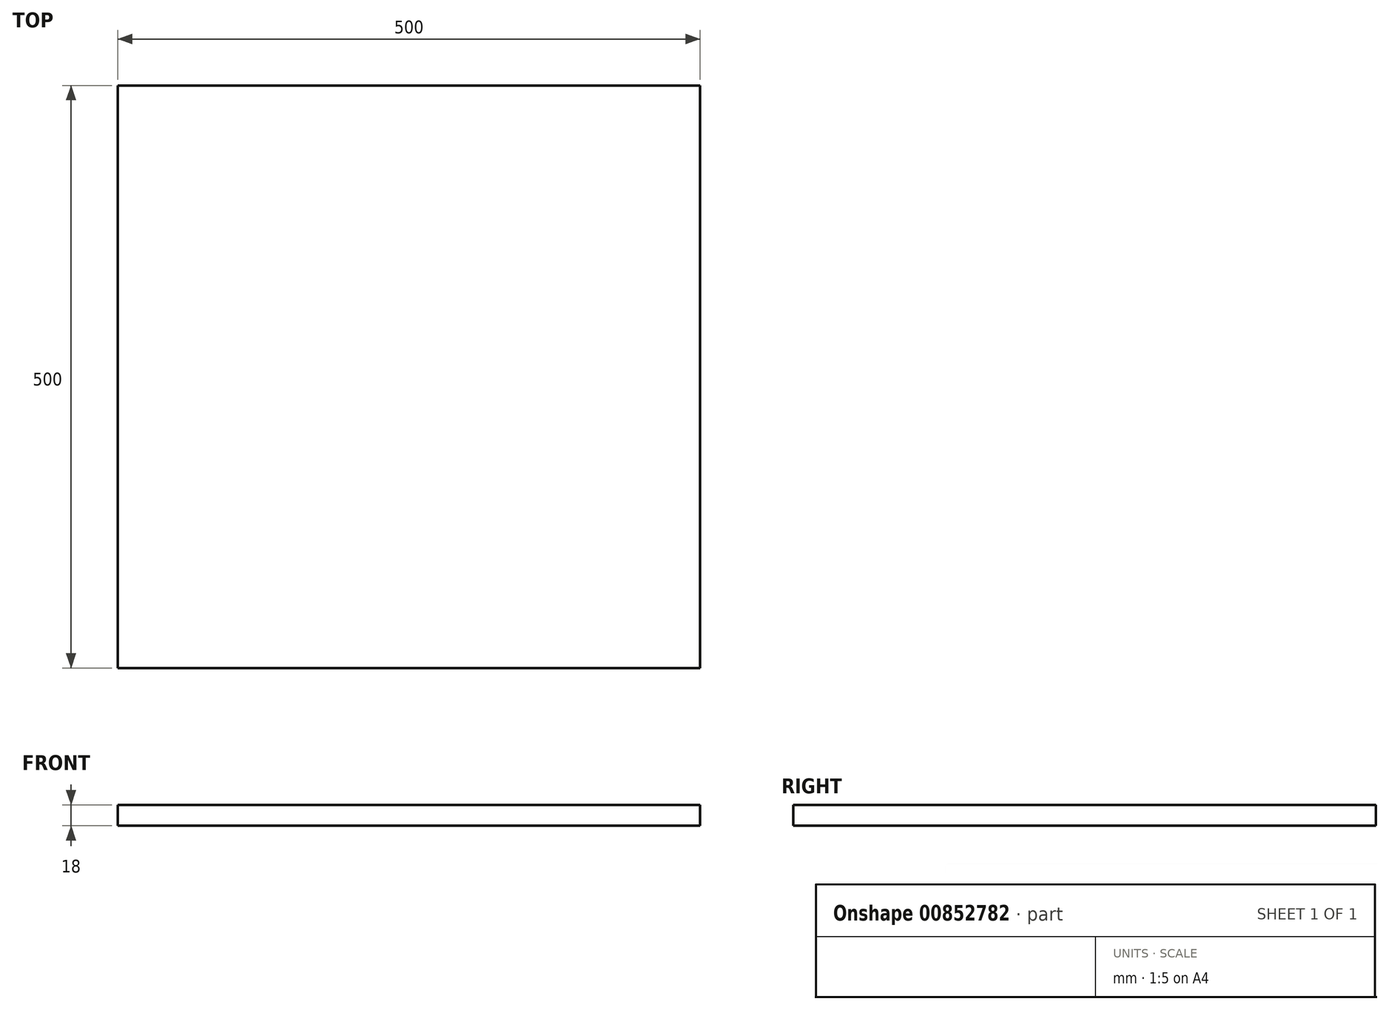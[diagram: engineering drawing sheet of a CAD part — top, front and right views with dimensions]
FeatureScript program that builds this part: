
annotation { "Feature Type Name" : "Feature", "Feature Type Description" : "" }
export const myFeature = defineFeature(function(context is Context, id is Id, definition is map)
    precondition{}
    {
        {
            var Q0;
            Q0=qCreatedBy(makeId("Top.planeOp"),FACE);
            var sketch = newSketch(context, id + "F0", { "sketchPlane" : qUnion([Q0])});
            skLineSegment(sketch, "E0.bottom", {"start": v(250, -250) * mm, "end": v(-250, -250) * mm});
            skLineSegment(sketch, "E0.top", {"start": v(250, 250) * mm, "end": v(-250, 250) * mm});
            skLineSegment(sketch, "E0.left", {"start": v(250, -250) * mm, "end": v(250, 250) * mm});
            skLineSegment(sketch, "E0.right", {"start": v(-250, -250) * mm, "end": v(-250, 250) * mm});
            skPoint(sketch, "E0.middle", {"position": v(0, 0) * mm});
            skSolve(sketch);
        }
        {
            var Q0;
            Q0 = qSketchRegion(id + "F0", true);
            extrude(context, id + "F1", {"entities" : qUnion([Q0]), "depth" : 18 * mm, "offsetDistance" : 25 * mm});
        }
    });
